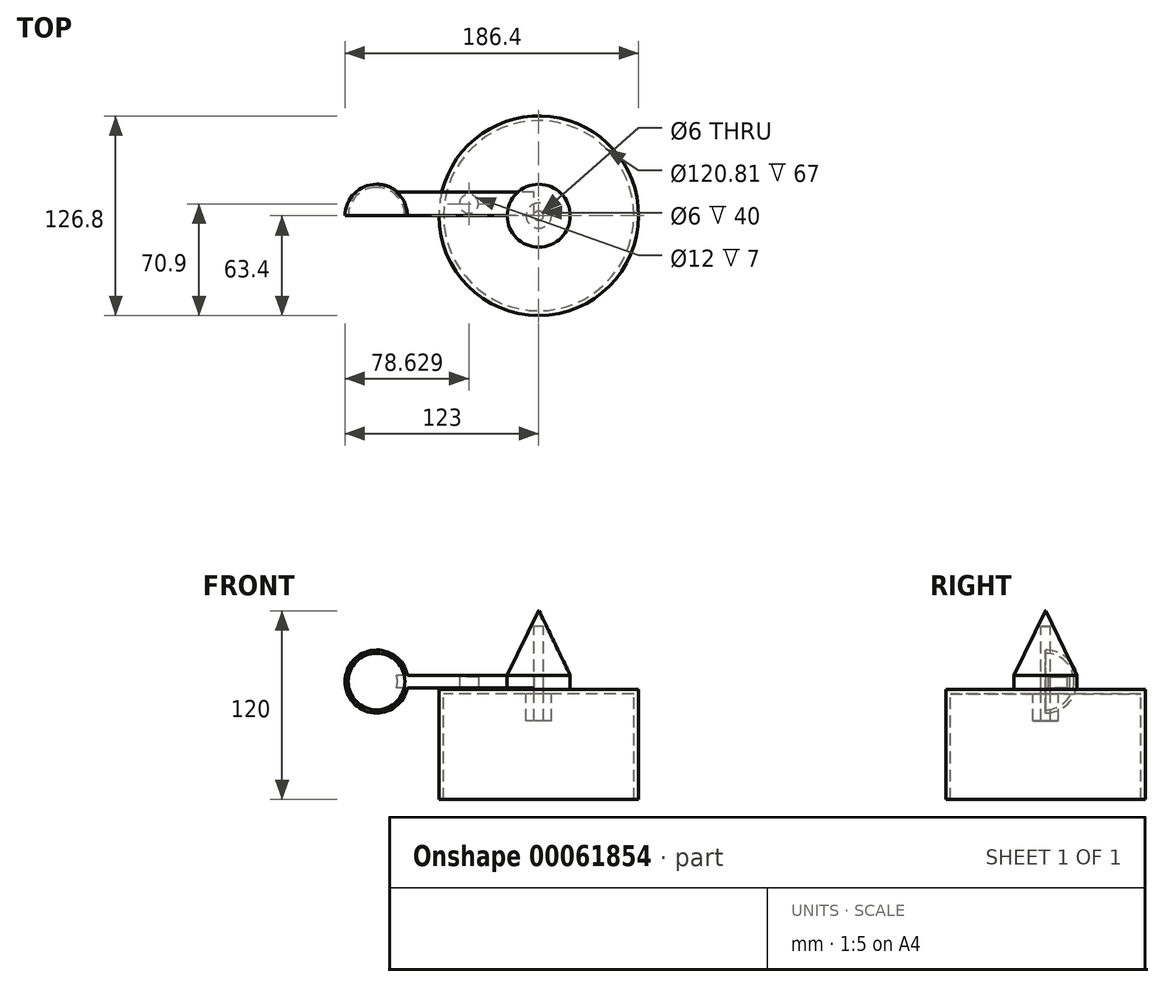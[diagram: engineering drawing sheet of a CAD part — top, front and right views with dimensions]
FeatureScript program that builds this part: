
annotation { "Feature Type Name" : "Feature", "Feature Type Description" : "" }
export const myFeature = defineFeature(function(context is Context, id is Id, definition is map)
    precondition{}
    {
        {
            var Q0;
            Q0=qCreatedBy(makeId("Top.planeOp"),FACE);
            var sketch = newSketch(context, id + "F0", { "sketchPlane" : qUnion([Q0])});
            skArc(sketch, "E0", {"start": v(0, 18) * mm, "mid": v(-12.73, 12.73) * mm, "end": v(-18, 0) * mm});
            skArc(sketch, "E1", {"start": v(-20, 0) * mm, "mid": v(-14.14, 14.14) * mm, "end": v(0, 20) * mm});
            skLineSegment(sketch, "E2", {"start": v(-20, 0) * mm, "end": v(-18, 0) * mm});
            skLineSegment(sketch, "E3", {"start": v(0, 20) * mm, "end": v(0, 18) * mm});
            skLineSegment(sketch, "E4", {"start": v(0, 18) * mm, "end": v(0, 0) * mm, "construction": true});
            skSolve(sketch);
        }
        {
            var Q0;
            Q0 = qSketchRegion(id + "F0", true);
            var Q1;
            Q1=sQuery(id+"F0.wireOp",EDGE,"E4");
            revolve(context, id + "F1", {"entities" : qUnion([Q0]), "axis" : qUnion([Q1]), "revolveType" : RevolveType.FULL});
        }
        {
            var Q0;
            Q0=qCreatedBy(makeId("Right.planeOp"),FACE);
            var sketch = newSketch(context, id + "F2", { "sketchPlane" : qUnion([Q0])});
            skLineSegment(sketch, "E5.bottom", {"start": v(0, -4) * mm, "end": v(15, -4) * mm});
            skLineSegment(sketch, "E5.top", {"start": v(0, 4) * mm, "end": v(15, 4) * mm});
            skLineSegment(sketch, "E5.left", {"start": v(0, 4) * mm, "end": v(0, -4) * mm});
            skLineSegment(sketch, "E5.right", {"start": v(15, 4) * mm, "end": v(15, -4) * mm});
            skSolve(sketch);
        }
        {
            var Q0;
            Q0 = qSketchRegion(id + "F2", true);
            extrude(context, id + "F3", {"entities" : qUnion([Q0]), "operationType" : NewBodyOperationType.ADD, "depth" : 100 * mm});
        }
        {
            var Q0;
            Q0=qCreatedBy(makeId("Top.planeOp"),FACE);
            var sketch = newSketch(context, id + "F4", { "sketchPlane" : qUnion([Q0])});
            skArc(sketch, "E6", {"start": v(-18, 0) * mm, "mid": v(-12.73, 12.73) * mm, "end": v(0, 18) * mm});
            skLineSegment(sketch, "E7", {"start": v(-18, 0) * mm, "end": v(0, 0) * mm});
            skLineSegment(sketch, "E8", {"start": v(0, 18) * mm, "end": v(0, 0) * mm});
            skSolve(sketch);
        }
        {
            var Q0;
            Q0 = qSketchRegion(id + "F4", true);
            var Q1;
            Q1=sQuery(id+"F4.wireOp",EDGE,"E8");
            revolve(context, id + "F5", {"operationType" : NewBodyOperationType.REMOVE, "entities" : qUnion([Q0]), "axis" : qUnion([Q1]), "revolveType" : RevolveType.FULL, "oppositeDirection" : true});
        }
        {
            var Q0;
            Q0=qCreatedBy(makeId("Front.planeOp"),FACE);
            var sketch = newSketch(context, id + "F6", { "sketchPlane" : qUnion([Q0])});
            skLineSegment(sketch, "E9", {"start": v(102.84, 45) * mm, "end": v(83, 4) * mm});
            skLineSegment(sketch, "E10", {"start": v(83, 4) * mm, "end": v(83, -5) * mm});
            skLineSegment(sketch, "E11", {"start": v(83, -5) * mm, "end": v(100, -5) * mm});
            skLineSegment(sketch, "E12", {"start": v(103, 45.33) * mm, "end": v(103, -5) * mm, "construction": true});
            skLineSegment(sketch, "E13", {"start": v(102.84, 45) * mm, "end": v(103, 45) * mm});
            skLineSegment(sketch, "E14", {"start": v(103, 45) * mm, "end": v(103, 35) * mm});
            skLineSegment(sketch, "E15", {"start": v(103, 35) * mm, "end": v(100, 35) * mm});
            skLineSegment(sketch, "E16", {"start": v(100, 35) * mm, "end": v(100, -5) * mm});
            skLineSegment(sketch, "E17", {"start": v(100, 35) * mm, "end": v(98, 35) * mm, "construction": true});
            skSolve(sketch);
        }
        {
            var Q0;
            Q0 = qSketchRegion(id + "F6", true);
            var Q1;
            Q1=sQuery(id+"F6.wireOp",EDGE,"E12");
            revolve(context, id + "F7", {"entities" : qUnion([Q0]), "axis" : qUnion([Q1]), "revolveType" : RevolveType.FULL});
        }
        {
            var Q0;
            Q0=qCreatedBy(makeId("Front.planeOp"),FACE);
            var sketch = newSketch(context, id + "F8", { "sketchPlane" : qUnion([Q0])});
            skLineSegment(sketch, "E18", {"start": v(100, -5) * mm, "end": v(39.6, -5) * mm});
            skLineSegment(sketch, "E19", {"start": v(39.6, -5) * mm, "end": v(39.6, -75) * mm});
            skLineSegment(sketch, "E20", {"start": v(39.6, -75) * mm, "end": v(42.6, -75) * mm});
            skLineSegment(sketch, "E21", {"start": v(42.6, -75) * mm, "end": v(42.6, -8) * mm});
            skLineSegment(sketch, "E22", {"start": v(42.6, -8) * mm, "end": v(95, -8) * mm});
            skLineSegment(sketch, "E23", {"start": v(95, -8) * mm, "end": v(95, -25) * mm});
            skLineSegment(sketch, "E24", {"start": v(95, -25) * mm, "end": v(100, -25) * mm});
            skLineSegment(sketch, "E25", {"start": v(100, -25) * mm, "end": v(100, -5) * mm});
            skLineSegment(sketch, "E26", {"start": v(69.8, -5) * mm, "end": v(69.8, -8) * mm, "construction": true});
            skSolve(sketch);
        }
        {
            var Q0;
            Q0 = qSketchRegion(id + "F8", true);
            var Q1;
            Q1=sQuery(id+"F6.wireOp",EDGE,"E12");
            revolve(context, id + "F9", {"entities" : qUnion([Q0]), "axis" : qUnion([Q1]), "revolveType" : RevolveType.FULL});
        }
        {
            var Q0;
            Q0=qCreatedBy(makeId("Top.planeOp"),FACE);
            var sketch = newSketch(context, id + "F10", { "sketchPlane" : qUnion([Q0])});
            skLineSegment(sketch, "E27", {"start": v(83, 0) * mm, "end": v(113, 17.32) * mm, "construction": true});
            skLineSegment(sketch, "E28", {"start": v(113, 17.32) * mm, "end": v(113, -17.32) * mm, "construction": true});
            skLineSegment(sketch, "E29", {"start": v(113, -17.32) * mm, "end": v(83, 0) * mm, "construction": true});
            skLineSegment(sketch, "E30", {"start": v(113, 17.32) * mm, "end": v(103, 0) * mm, "construction": true});
            skLineSegment(sketch, "E31", {"start": v(103, 0) * mm, "end": v(113, -17.32) * mm, "construction": true});
            skLineSegment(sketch, "E32", {"start": v(103, 0) * mm, "end": v(83, 0) * mm, "construction": true});
            skSolve(sketch);
        }
        {
            var Q0;
            Q0=qCreatedBy(makeId("Top.planeOp"),FACE);
            var sketch = newSketch(context, id + "F11", { "sketchPlane" : qUnion([Q0])});
            skLineSegment(sketch, "E33", {"start": v(103, 0) * mm, "end": v(58.63, 7.5) * mm, "construction": true});
            skLineSegment(sketch, "E34", {"start": v(58.63, 0) * mm, "end": v(58.63, 15) * mm, "construction": true});
            skSolve(sketch);
        }
        {
            var Q0;
            Q0=qCreatedBy(makeId("Top.planeOp"),FACE);
            var sketch = newSketch(context, id + "F12", { "sketchPlane" : qUnion([Q0])});
            skCircle(sketch, "E35", {"center": v(58.63, 7.5) * mm, "radius": 6 * mm});
            skSolve(sketch);
        }
        {
            var Q0;
            Q0 = qSketchRegion(id + "F12", true);
            extrude(context, id + "F13", {"entities" : qUnion([Q0]), "operationType" : NewBodyOperationType.REMOVE, "depth" : 3 * mm, "hasSecondDirection" : true, "secondDirectionBound" : SecondDirectionBoundingType.UP_TO_NEXT, "secondDirectionOppositeDirection" : true, "secondDirectionDepth" : 25 * mm});
        }
    });
